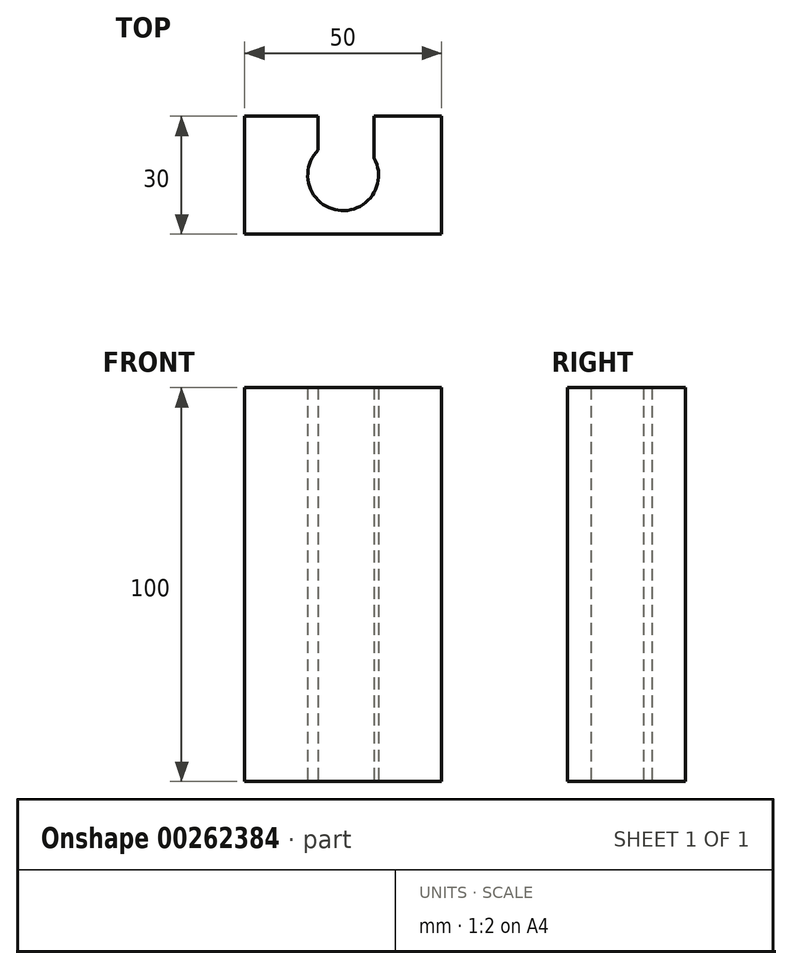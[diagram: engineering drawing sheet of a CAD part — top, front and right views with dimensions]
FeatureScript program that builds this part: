
annotation { "Feature Type Name" : "Feature", "Feature Type Description" : "" }
export const myFeature = defineFeature(function(context is Context, id is Id, definition is map)
    precondition{}
    {
        {
            var Q0;
            Q0=qCreatedBy(makeId("Top.planeOp"),FACE);
            var sketch = newSketch(context, id + "F0", { "sketchPlane" : qUnion([Q0])});
            skLineSegment(sketch, "E0.bottom", {"start": v(25, -15) * mm, "end": v(-25, -15) * mm});
            skLineSegment(sketch, "E0.top", {"start": v(25, 15) * mm, "end": v(-25, 15) * mm});
            skLineSegment(sketch, "E0.left", {"start": v(25, -15) * mm, "end": v(25, 15) * mm});
            skLineSegment(sketch, "E0.right", {"start": v(-25, -15) * mm, "end": v(-25, 15) * mm});
            skPoint(sketch, "E0.middle", {"position": v(0, 0) * mm});
            skCircle(sketch, "E1", {"center": v(0, 0) * mm, "radius": 9 * mm});
            skLineSegment(sketch, "E2", {"start": v(-6.34, 6.4) * mm, "end": v(-6.34, 15) * mm});
            skLineSegment(sketch, "E3", {"start": v(-6.34, 15) * mm, "end": v(7.9, 15) * mm});
            skLineSegment(sketch, "E4", {"start": v(7.9, 15) * mm, "end": v(7.9, 4.32) * mm});
            skLineSegment(sketch, "E5", {"start": v(7.9, 4.32) * mm, "end": v(-6.34, 6.4) * mm});
            skSolve(sketch);
        }
        {
            var Q0;
            Q0=makeQuery(id+"F0.imprint","IMPRINT",FACE,{"disambiguationData":[TD([[makeQuery(id+"F0.imprint","IMPRINT",EDGE,{"derivedFrom":sQuery(id+"F0.wireOp",EDGE,"E0.bottom")}),-1.0]])]});
            extrude(context, id + "F1", {"entities" : qUnion([Q0]), "depth" : 100 * mm});
        }
    });
